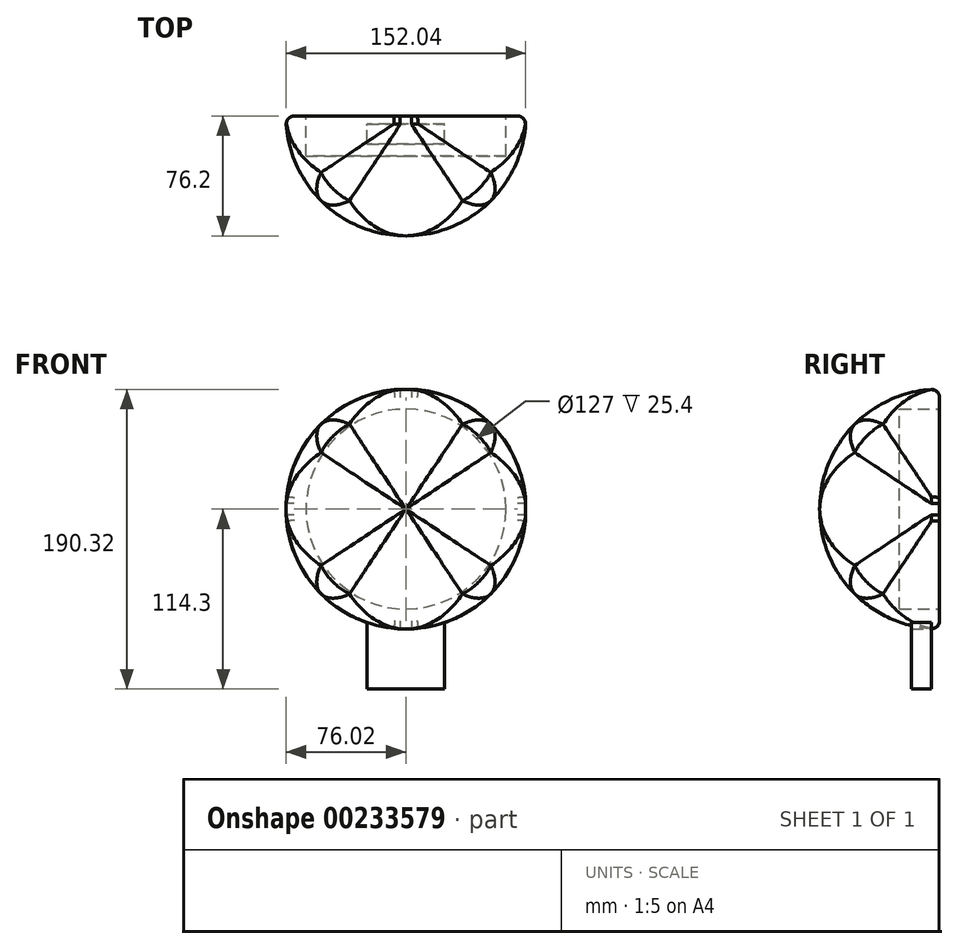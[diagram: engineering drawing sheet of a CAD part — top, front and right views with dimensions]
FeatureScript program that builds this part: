
annotation { "Feature Type Name" : "Feature", "Feature Type Description" : "" }
export const myFeature = defineFeature(function(context is Context, id is Id, definition is map)
    precondition{}
    {
        {
            var Q0;
            Q0=qCreatedBy(makeId("Front.planeOp"),FACE);
            var sketch = newSketch(context, id + "F0", { "sketchPlane" : qUnion([Q0])});
            skCircle(sketch, "E0", {"center": v(0, 0) * mm, "radius": 76.2 * mm});
            skCircle(sketch, "E1", {"center": v(0, 0) * mm, "radius": 63.5 * mm});
            skLineSegment(sketch, "E2", {"start": v(0, -114.3) * mm, "end": v(24.6, -114.3) * mm});
            skLineSegment(sketch, "E3", {"start": v(24.6, -114.3) * mm, "end": v(24.6, -72.12) * mm});
            skLineSegment(sketch, "E4.MirrorCS", {"start": v(0, -114.3) * mm, "end": v(-24.6, -114.3) * mm});
            skLineSegment(sketch, "E5.MirrorCS", {"start": v(-24.6, -114.3) * mm, "end": v(-24.6, -72.12) * mm});
            skPoint(sketch, "E6.start.orphan", {"position": v(0, -76.2) * mm});
            skSolve(sketch);
        }
        {
            var Q0;
            Q0=qCreatedBy(makeId("Top.planeOp"),FACE);
            var sketch = newSketch(context, id + "F1", { "sketchPlane" : qUnion([Q0])});
            skCircle(sketch, "E7", {"center": v(0, 0) * mm, "radius": 76.2 * mm});
            skLineSegment(sketch, "E8", {"start": v(76.2, 0) * mm, "end": v(84.96, -95.98) * mm});
            skLineSegment(sketch, "E9", {"start": v(84.96, -95.98) * mm, "end": v(-113.54, -82.25) * mm});
            skLineSegment(sketch, "E10", {"start": v(-113.54, -82.25) * mm, "end": v(-76.2, 0) * mm});
            skLineSegment(sketch, "E11", {"start": v(-76.2, 0) * mm, "end": v(-145.63, 41.79) * mm});
            skSolve(sketch);
        }
        {
            var Q0;
            Q0=qCreatedBy(makeId("Right.planeOp"),FACE);
            var sketch = newSketch(context, id + "F2", { "sketchPlane" : qUnion([Q0])});
            skCircle(sketch, "E12", {"center": v(0, 0) * mm, "radius": 76.2 * mm});
            skLineSegment(sketch, "E13", {"start": v(0, 76.2) * mm, "end": v(-82.17, 76.2) * mm});
            skLineSegment(sketch, "E14", {"start": v(-82.17, 76.2) * mm, "end": v(-76.42, 0) * mm});
            skLineSegment(sketch, "E15", {"start": v(-76.42, 0) * mm, "end": v(-90.11, -87.22) * mm});
            skLineSegment(sketch, "E16", {"start": v(-90.11, -87.22) * mm, "end": v(0, -76.72) * mm});
            skLineSegment(sketch, "E17", {"start": v(0, -76.72) * mm, "end": v(0, 76.2) * mm});
            skSolve(sketch);
        }
        {
            var Q0;
            Q0=makeQuery(id+"F0.imprint","IMPRINT",FACE,{"disambiguationData":[TD([[makeQuery(id+"F0.imprint","IMPRINT",EDGE,{"derivedFrom":sQuery(id+"F0.wireOp",EDGE,"E0")}),1.0]])]});
            var Q1;
            Q1=makeQuery(id+"F0.imprint","IMPRINT",FACE,{"disambiguationData":[TD([[makeQuery(id+"F0.imprint","IMPRINT",EDGE,{"derivedFrom":sQuery(id+"F0.wireOp",EDGE,"E1")}),1.0]])]});
            extrude(context, id + "F3", {"entities" : qUnion([Q0, Q1]), "depth" : 76.2 * mm});
        }
        {
            var Q0;
            {var subQ0=sQuery(id+"F2.wireOp",EDGE,"E13");Q0=makeQuery(id+"F2.imprint","IMPRINT",FACE,{"disambiguationData":[TD([[makeQuery(id+"F2.imprint","IMPRINT",EDGE,{"derivedFrom":subQ0}),1.0]])]});}
            extrude(context, id + "F4", {"entities" : qUnion([Q0]), "operationType" : NewBodyOperationType.REMOVE, "endBound" : BoundingType.SYMMETRIC, "oppositeDirection" : true, "depth" : 177.8 * mm});
        }
        {
            var Q0;
            {var subQ0=sQuery(id+"F1.wireOp",EDGE,"E8");Q0=makeQuery(id+"F1.imprint","IMPRINT",FACE,{"disambiguationData":[TD([[makeQuery(id+"F1.imprint","IMPRINT",EDGE,{"derivedFrom":subQ0}),-1.0]])]});}
            extrude(context, id + "F5", {"entities" : qUnion([Q0]), "operationType" : NewBodyOperationType.REMOVE, "endBound" : BoundingType.SYMMETRIC, "oppositeDirection" : true, "depth" : 152.4 * mm});
        }
        {
            var Q0;
            Q0=makeQuery(id+"F5.boolean.opBoolean","INTERSECT",EDGE,{"disambiguationData":[OD(1.0)],"derivedFrom":[makeQuery(id+"F4.boolean.opBoolean","SPLIT",FACE,{"disambiguationData":[OD(1.0)],"derivedFrom":makeQuery(id+"F3.opExtrude","SWEPT_FACE",FACE,{"disambiguationData":[OSD([sQuery(id+"F0.wireOp",EDGE,"E0")])]})}),makeQuery(id+"F5.opExtrude","SWEPT_FACE",FACE,{"disambiguationData":[OSD([sQuery(id+"F1.wireOp",EDGE,"E7")])]})]});
            var Q1;
            Q1=makeQuery(id+"F5.boolean.opBoolean","SPLIT",EDGE,{"disambiguationData":[OD(1.0)],"derivedFrom":makeQuery(id+"F4.boolean.opBoolean","INTERSECT",EDGE,{"disambiguationData":[OD(1.0)],"derivedFrom":[makeQuery(id+"F3.opExtrude","SWEPT_FACE",FACE,{"disambiguationData":[OSD([sQuery(id+"F0.wireOp",EDGE,"E0")])]}),makeQuery(id+"F4.opExtrude","SWEPT_FACE",FACE,{"disambiguationData":[OSD([sQuery(id+"F2.wireOp",EDGE,"E12")])]})]})});
            var Q2;
            Q2=makeQuery(id+"F5.boolean.opBoolean","INTERSECT",EDGE,{"disambiguationData":[OD(3.0)],"derivedFrom":[makeQuery(id+"F4.boolean.opBoolean","COPY",FACE,{"derivedFrom":makeQuery(id+"F4.opExtrude","SWEPT_FACE",FACE,{"disambiguationData":[OSD([sQuery(id+"F2.wireOp",EDGE,"E12")])]})}),makeQuery(id+"F5.opExtrude","SWEPT_FACE",FACE,{"disambiguationData":[OSD([sQuery(id+"F1.wireOp",EDGE,"E7")])]})]});
            var Q3;
            Q3=makeQuery(id+"F5.boolean.opBoolean","INTERSECT",EDGE,{"disambiguationData":[OD(0.0)],"derivedFrom":[makeQuery(id+"F4.boolean.opBoolean","SPLIT",FACE,{"disambiguationData":[OD(1.0)],"derivedFrom":makeQuery(id+"F3.opExtrude","SWEPT_FACE",FACE,{"disambiguationData":[OSD([sQuery(id+"F0.wireOp",EDGE,"E0")])]})}),makeQuery(id+"F5.opExtrude","SWEPT_FACE",FACE,{"disambiguationData":[OSD([sQuery(id+"F1.wireOp",EDGE,"E7")])]})]});
            var Q4;
            Q4=makeQuery(id+"F5.boolean.opBoolean","INTERSECT",EDGE,{"disambiguationData":[OD(2.0)],"derivedFrom":[makeQuery(id+"F4.boolean.opBoolean","COPY",FACE,{"derivedFrom":makeQuery(id+"F4.opExtrude","SWEPT_FACE",FACE,{"disambiguationData":[OSD([sQuery(id+"F2.wireOp",EDGE,"E12")])]})}),makeQuery(id+"F5.opExtrude","SWEPT_FACE",FACE,{"disambiguationData":[OSD([sQuery(id+"F1.wireOp",EDGE,"E7")])]})]});
            var Q5;
            Q5=makeQuery(id+"F5.boolean.opBoolean","INTERSECT",EDGE,{"disambiguationData":[OD(0.0)],"derivedFrom":[makeQuery(id+"F4.boolean.opBoolean","COPY",FACE,{"derivedFrom":makeQuery(id+"F4.opExtrude","SWEPT_FACE",FACE,{"disambiguationData":[OSD([sQuery(id+"F2.wireOp",EDGE,"E12")])]})}),makeQuery(id+"F5.opExtrude","SWEPT_FACE",FACE,{"disambiguationData":[OSD([sQuery(id+"F1.wireOp",EDGE,"E7")])]})]});
            var Q6;
            Q6=makeQuery(id+"F5.boolean.opBoolean","INTERSECT",EDGE,{"disambiguationData":[OD(1.0)],"derivedFrom":[makeQuery(id+"F4.boolean.opBoolean","COPY",FACE,{"derivedFrom":makeQuery(id+"F4.opExtrude","SWEPT_FACE",FACE,{"disambiguationData":[OSD([sQuery(id+"F2.wireOp",EDGE,"E12")])]})}),makeQuery(id+"F5.opExtrude","SWEPT_FACE",FACE,{"disambiguationData":[OSD([sQuery(id+"F1.wireOp",EDGE,"E7")])]})]});
            var Q7;
            Q7=makeQuery(id+"F5.boolean.opBoolean","SPLIT",EDGE,{"disambiguationData":[OD(1.0)],"derivedFrom":makeQuery(id+"F4.boolean.opBoolean","INTERSECT",EDGE,{"disambiguationData":[OD(0.0)],"derivedFrom":[makeQuery(id+"F3.opExtrude","SWEPT_FACE",FACE,{"disambiguationData":[OSD([sQuery(id+"F0.wireOp",EDGE,"E0")])]}),makeQuery(id+"F4.opExtrude","SWEPT_FACE",FACE,{"disambiguationData":[OSD([sQuery(id+"F2.wireOp",EDGE,"E12")])]})]})});
            var Q8;
            Q8=makeQuery(id+"F5.boolean.opBoolean","INTERSECT",EDGE,{"disambiguationData":[OD(1.0)],"derivedFrom":[makeQuery(id+"F4.boolean.opBoolean","SPLIT",FACE,{"disambiguationData":[OD(0.0)],"derivedFrom":makeQuery(id+"F3.opExtrude","SWEPT_FACE",FACE,{"disambiguationData":[OSD([sQuery(id+"F0.wireOp",EDGE,"E0")])]})}),makeQuery(id+"F5.opExtrude","SWEPT_FACE",FACE,{"disambiguationData":[OSD([sQuery(id+"F1.wireOp",EDGE,"E7")])]})]});
            var Q9;
            Q9=makeQuery(id+"F5.boolean.opBoolean","INTERSECT",EDGE,{"disambiguationData":[OD(0.0)],"derivedFrom":[makeQuery(id+"F4.boolean.opBoolean","SPLIT",FACE,{"disambiguationData":[OD(0.0)],"derivedFrom":makeQuery(id+"F3.opExtrude","SWEPT_FACE",FACE,{"disambiguationData":[OSD([sQuery(id+"F0.wireOp",EDGE,"E0")])]})}),makeQuery(id+"F5.opExtrude","SWEPT_FACE",FACE,{"disambiguationData":[OSD([sQuery(id+"F1.wireOp",EDGE,"E7")])]})]});
            var Q10;
            Q10=makeQuery(id+"F5.boolean.opBoolean","SPLIT",EDGE,{"disambiguationData":[OD(0.0)],"derivedFrom":makeQuery(id+"F4.boolean.opBoolean","INTERSECT",EDGE,{"disambiguationData":[OD(0.0)],"derivedFrom":[makeQuery(id+"F3.opExtrude","SWEPT_FACE",FACE,{"disambiguationData":[OSD([sQuery(id+"F0.wireOp",EDGE,"E0")])]}),makeQuery(id+"F4.opExtrude","SWEPT_FACE",FACE,{"disambiguationData":[OSD([sQuery(id+"F2.wireOp",EDGE,"E12")])]})]})});
            var Q11;
            Q11=makeQuery(id+"F5.boolean.opBoolean","SPLIT",EDGE,{"disambiguationData":[OD(0.0)],"derivedFrom":makeQuery(id+"F4.boolean.opBoolean","INTERSECT",EDGE,{"disambiguationData":[OD(1.0)],"derivedFrom":[makeQuery(id+"F3.opExtrude","SWEPT_FACE",FACE,{"disambiguationData":[OSD([sQuery(id+"F0.wireOp",EDGE,"E0")])]}),makeQuery(id+"F4.opExtrude","SWEPT_FACE",FACE,{"disambiguationData":[OSD([sQuery(id+"F2.wireOp",EDGE,"E12")])]})]})});
            fillet(context, id + "F6", {"entities" : qUnion([Q0, Q1, Q2, Q3, Q4, Q5, Q6, Q7, Q8, Q9, Q10, Q11]), "radius" : 25.4 * mm, "tangentPropagation" : true, "allowEdgeOverflow" : false});
        }
        {
            var Q0;
            Q0=makeQuery(id+"F0.imprint","IMPRINT",FACE,{"disambiguationData":[TD([[makeQuery(id+"F0.imprint","IMPRINT",EDGE,{"derivedFrom":sQuery(id+"F0.wireOp",EDGE,"E1")}),1.0]])]});
            extrude(context, id + "F7", {"entities" : qUnion([Q0]), "operationType" : NewBodyOperationType.REMOVE, "depth" : 25.4 * mm});
        }
        {
            var Q0;
            Q0=makeQuery(id+"F7.boolean.opBoolean","COPY",EDGE,{"derivedFrom":makeQuery(id+"F7.opExtrude","CAP_EDGE",EDGE,{"disambiguationData":[OSD([sQuery(id+"F0.wireOp",EDGE,"E1")])],"isStart":true})});
            var Q1;
            Q1=makeQuery(id+"F5.boolean.opBoolean","SPLIT",EDGE,{"disambiguationData":[OD(0.0)],"derivedFrom":makeQuery(id+"F4.boolean.opBoolean","SPLIT",EDGE,{"disambiguationData":[OD(0.0)],"derivedFrom":makeQuery(id+"F3.opExtrude","CAP_EDGE",EDGE,{"disambiguationData":[OSD([sQuery(id+"F0.wireOp",EDGE,"E0")])],"isStart":true})})});
            var Q2;
            Q2=makeQuery(id+"F5.boolean.opBoolean","SPLIT",EDGE,{"disambiguationData":[OD(1.0)],"derivedFrom":makeQuery(id+"F4.boolean.opBoolean","SPLIT",EDGE,{"disambiguationData":[OD(0.0)],"derivedFrom":makeQuery(id+"F3.opExtrude","CAP_EDGE",EDGE,{"disambiguationData":[OSD([sQuery(id+"F0.wireOp",EDGE,"E0")])],"isStart":true})})});
            var Q3;
            Q3=makeQuery(id+"F5.boolean.opBoolean","SPLIT",EDGE,{"disambiguationData":[OD(1.0)],"derivedFrom":makeQuery(id+"F4.boolean.opBoolean","SPLIT",EDGE,{"disambiguationData":[OD(1.0)],"derivedFrom":makeQuery(id+"F3.opExtrude","CAP_EDGE",EDGE,{"disambiguationData":[OSD([sQuery(id+"F0.wireOp",EDGE,"E0")])],"isStart":true})})});
            var Q4;
            Q4=makeQuery(id+"F5.boolean.opBoolean","SPLIT",EDGE,{"disambiguationData":[OD(0.0)],"derivedFrom":makeQuery(id+"F4.boolean.opBoolean","SPLIT",EDGE,{"disambiguationData":[OD(1.0)],"derivedFrom":makeQuery(id+"F3.opExtrude","CAP_EDGE",EDGE,{"disambiguationData":[OSD([sQuery(id+"F0.wireOp",EDGE,"E0")])],"isStart":true})})});
            fillet(context, id + "F8", {"entities" : qUnion([Q0, Q1, Q2, Q3, Q4]), "radius" : 5.08 * mm, "tangentPropagation" : true, "allowEdgeOverflow" : false});
        }
        {
            var Q0;
            Q0=makeQuery(id+"F0.imprint","IMPRINT",FACE,{"disambiguationData":[TD([[makeQuery(id+"F0.imprint","IMPRINT",EDGE,{"derivedFrom":sQuery(id+"F0.wireOp",EDGE,"E2")}),1.0]])]});
            extrude(context, id + "F9", {"entities" : qUnion([Q0]), "operationType" : NewBodyOperationType.ADD, "depth" : 17.78 * mm});
        }
        {
            var Q0;
            Q0=makeQuery(id+"F9.opExtrude","CAP_FACE",FACE,{"disambiguationData":[OSD([sQuery(id+"F0.wireOp",EDGE,"E0"),sQuery(id+"F0.wireOp",EDGE,"E2"),sQuery(id+"F0.wireOp",EDGE,"E3"),sQuery(id+"F0.wireOp",EDGE,"E4.MirrorCS"),sQuery(id+"F0.wireOp",EDGE,"E5.MirrorCS")])],"isStart":true});
            extrude(context, id + "F10", {"entities" : qUnion([Q0]), "operationType" : NewBodyOperationType.REMOVE, "oppositeDirection" : true, "depth" : 5.08 * mm});
        }
    });
